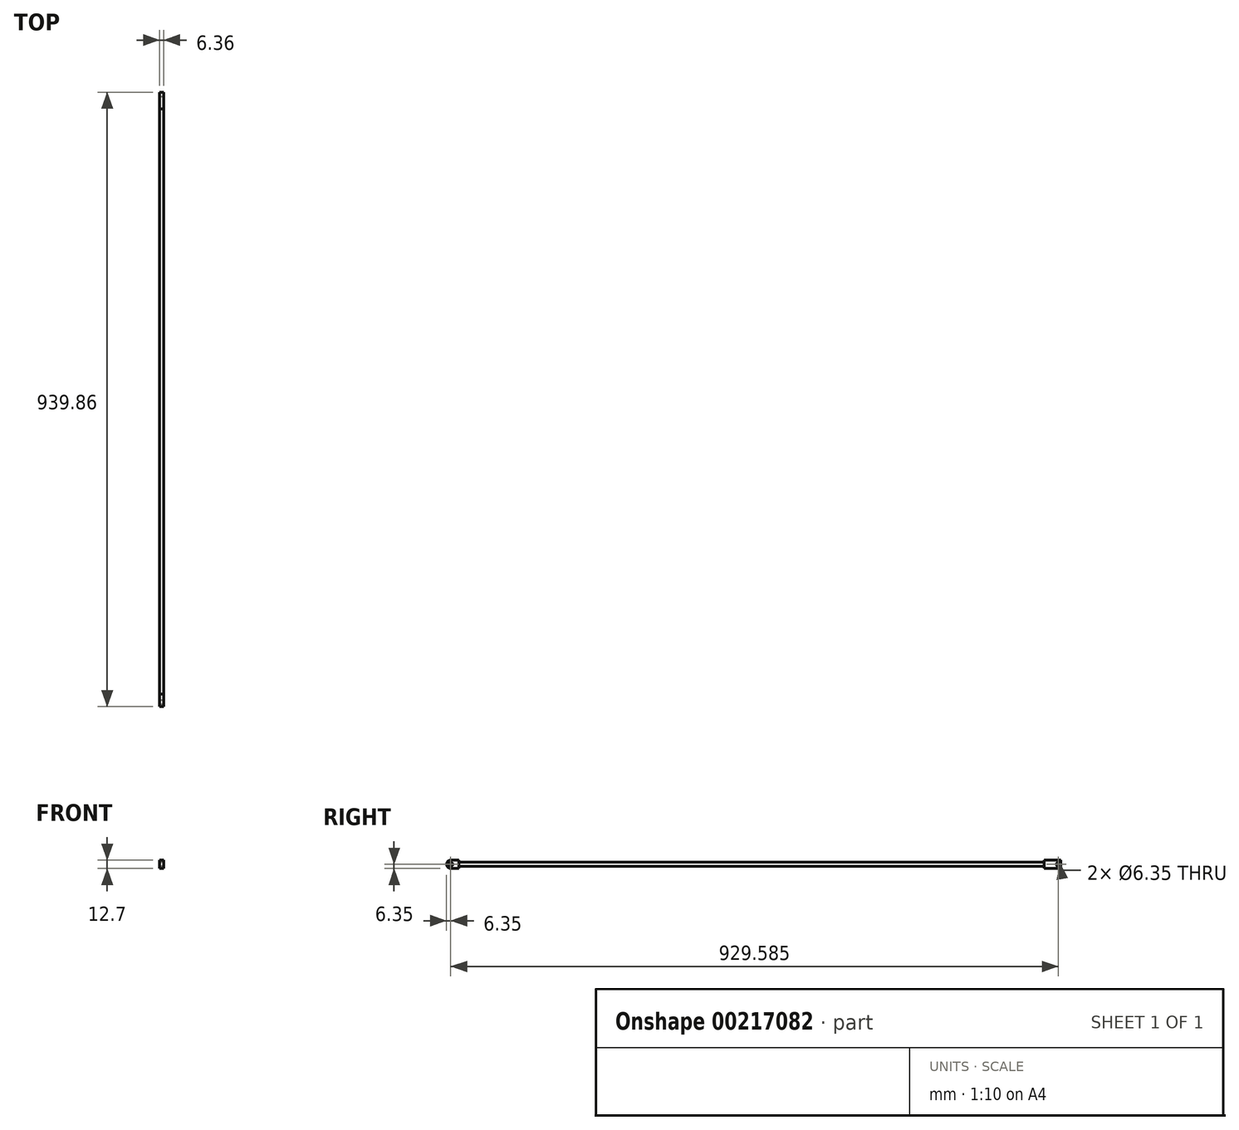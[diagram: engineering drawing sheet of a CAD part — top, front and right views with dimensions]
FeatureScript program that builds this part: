
annotation { "Feature Type Name" : "Feature", "Feature Type Description" : "" }
export const myFeature = defineFeature(function(context is Context, id is Id, definition is map)
    precondition{}
    {
        {
            var Q0;
            Q0=qCreatedBy(makeId("Front.planeOp"),FACE);
            var sketch = newSketch(context, id + "F0", { "sketchPlane" : qUnion([Q0])});
            skCircle(sketch, "E0", {"center": v(0, 0) * mm, "radius": 3.18 * mm});
            skSolve(sketch);
        }
        {
            var Q0;
            Q0=qCreatedBy(makeId("Right.planeOp"),FACE);
            var sketch = newSketch(context, id + "F1", { "sketchPlane" : qUnion([Q0])});
            skLineSegment(sketch, "E1.bottom", {"start": v(6.35, -6.35) * mm, "end": v(-6.35, -6.35) * mm});
            skLineSegment(sketch, "E1.top", {"start": v(6.35, 6.35) * mm, "end": v(-6.35, 6.35) * mm});
            skLineSegment(sketch, "E1.left", {"start": v(6.35, -6.35) * mm, "end": v(6.35, 6.35) * mm});
            skPoint(sketch, "E1.middle", {"position": v(0, 0) * mm});
            skCircle(sketch, "E2", {"center": v(-6.35, 0) * mm, "radius": 6.35 * mm});
            skCircle(sketch, "E3", {"center": v(-6.35, 0) * mm, "radius": 3.18 * mm});
            skSolve(sketch);
        }
        {
            var Q0;
            Q0=makeQuery(id+"F1.imprint","IMPRINT",FACE,{"disambiguationData":[TD([[makeQuery(id+"F1.imprint","IMPRINT",EDGE,{"derivedFrom":sQuery(id+"F1.wireOp",EDGE,"E3")}),-1.0]])]});
            extrude(context, id + "F2", {"entities" : qUnion([Q0]), "depth" : 6.35 * mm, "symmetric" : true});
        }
        {
            var Q0;
            {var subQ0=sQuery(id+"F1.wireOp",EDGE,"E1.bottom");Q0=makeQuery(id+"F1.imprint","IMPRINT",FACE,{"disambiguationData":[TD([[makeQuery(id+"F1.imprint","IMPRINT",EDGE,{"derivedFrom":subQ0}),-1.0]])]});}
            extrude(context, id + "F3", {"entities" : qUnion([Q0]), "operationType" : NewBodyOperationType.ADD, "depth" : 6.35 * mm, "symmetric" : true});
        }
        {
            var Q0;
            Q0 = qSketchRegion(id + "F0", true);
            var Q1;
            Q1=sQuery(id+"F0.wireOp",EDGE,"E0");
            extrude(context, id + "F4", {"entities" : qUnion([Q0]), "operationType" : NewBodyOperationType.ADD, "surfaceEntities" : qUnion([Q1]), "oppositeDirection" : true, "depth" : 914.4 * mm});
        }
        {
            var Q0;
            Q0=qCreatedBy(makeId("Right.planeOp"),FACE);
            var sketch = newSketch(context, id + "F5", { "sketchPlane" : qUnion([Q0])});
            skLineSegment(sketch, "E4.bottom", {"start": v(927.16, -6.35) * mm, "end": v(901.76, -6.35) * mm});
            skLineSegment(sketch, "E4.top", {"start": v(927.16, 6.35) * mm, "end": v(901.76, 6.35) * mm});
            skLineSegment(sketch, "E4.left", {"start": v(927.16, -6.35) * mm, "end": v(927.16, 6.35) * mm});
            skLineSegment(sketch, "E4.right", {"start": v(901.76, -6.35) * mm, "end": v(901.76, 6.35) * mm});
            skPoint(sketch, "E4.middle", {"position": v(914.46, 0) * mm});
            skCircle(sketch, "E5", {"center": v(923.23, 0) * mm, "radius": 3.18 * mm});
            skPoint(sketch, "E5.centerSnap0", {"position": v(927.16, 0) * mm});
            skSolve(sketch);
        }
        {
            var Q0;
            Q0=makeQuery(id+"F5.imprint","IMPRINT",FACE,{"disambiguationData":[TD([[makeQuery(id+"F5.imprint","IMPRINT",EDGE,{"derivedFrom":sQuery(id+"F5.wireOp",EDGE,"E4.bottom")}),-1.0]])]});
            extrude(context, id + "F6", {"entities" : qUnion([Q0]), "operationType" : NewBodyOperationType.ADD, "depth" : 6.35 * mm, "symmetric" : true});
        }
    });
